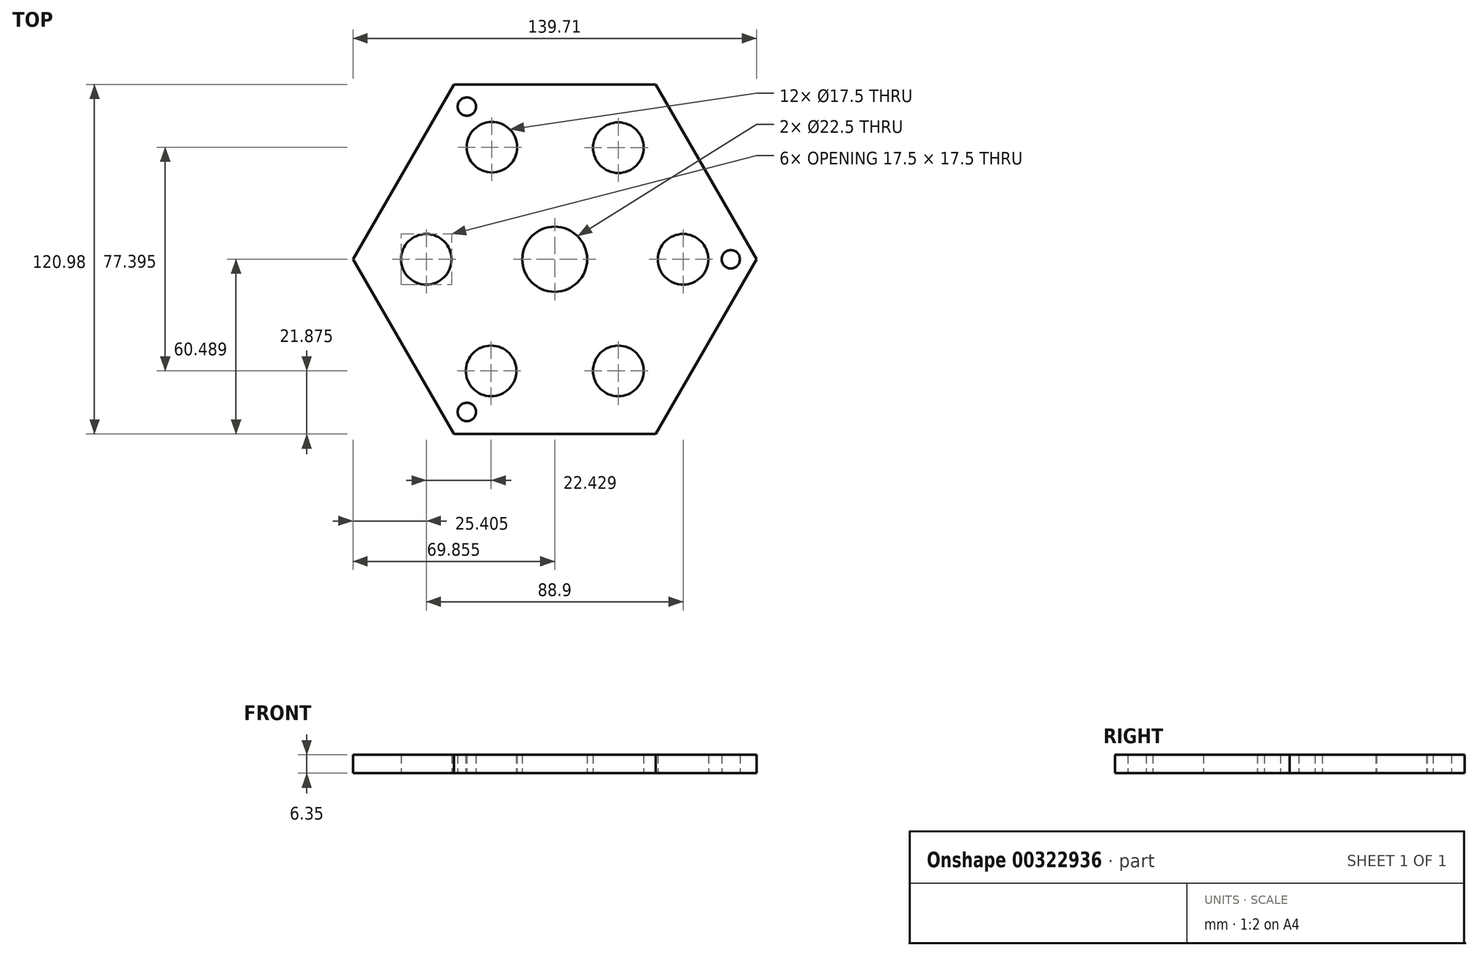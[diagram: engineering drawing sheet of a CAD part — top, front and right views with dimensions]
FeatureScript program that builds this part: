
annotation { "Feature Type Name" : "Feature", "Feature Type Description" : "" }
export const myFeature = defineFeature(function(context is Context, id is Id, definition is map)
    precondition{}
    {
        {
            var Q0;
            Q0=qCreatedBy(makeId("Top.planeOp"),FACE);
            var sketch = newSketch(context, id + "F0", { "sketchPlane" : qUnion([Q0])});
            skLineSegment(sketch, "E0.0", {"start": v(-31.75, 66) * mm, "end": v(38.1, 66) * mm});
            skLineSegment(sketch, "E0.1", {"start": v(38.1, 66) * mm, "end": v(73.02, 5.5) * mm});
            skLineSegment(sketch, "E0.2", {"start": v(73.03, 5.5) * mm, "end": v(38.1, -55) * mm});
            skLineSegment(sketch, "E0.3", {"start": v(38.1, -55) * mm, "end": v(-31.75, -55) * mm});
            skLineSegment(sketch, "E0.4", {"start": v(-31.75, -55) * mm, "end": v(-66.68, 5.5) * mm});
            skLineSegment(sketch, "E0.5", {"start": v(-66.67, 5.5) * mm, "end": v(-31.75, 66) * mm});
            skPoint(sketch, "E1", {"position": v(-41.27, 5.5) * mm});
            skPoint(sketch, "E2", {"position": v(-18.85, -33.11) * mm});
            skPoint(sketch, "E3", {"position": v(25.2, 44.11) * mm});
            skPoint(sketch, "E4", {"position": v(-18.57, 44.28) * mm});
            skPoint(sketch, "E5", {"position": v(47.62, 5.5) * mm});
            skPoint(sketch, "E6", {"position": v(25.2, -33.11) * mm});
            skPoint(sketch, "E7", {"position": v(-31.75, 66) * mm});
            skPoint(sketch, "E8", {"position": v(-27.23, 58.33) * mm});
            skPoint(sketch, "E9", {"position": v(-27.23, -47.34) * mm});
            skPoint(sketch, "E10", {"position": v(64.13, 5.5) * mm});
            skPoint(sketch, "E11", {"position": v(0, 0) * mm});
            skLineSegment(sketch, "E12", {"start": v(-18.85, -33.11) * mm, "end": v(25.2, 44.11) * mm});
            skPoint(sketch, "E13", {"position": v(3.17, 5.5) * mm});
            skSolve(sketch);
        }
        {
            var Q0;
            Q0=makeQuery(id+"F0.imprint","IMPRINT",FACE,{"disambiguationData":[TD([[makeQuery(id+"F0.imprint","IMPRINT",EDGE,{"derivedFrom":sQuery(id+"F0.wireOp",EDGE,"E0.0")}),-1.0]])]});
            extrude(context, id + "F1", {"entities" : qUnion([Q0]), "depth" : 6.35 * mm});
        }
        {
            var Q0;
            Q0=sQuery(id+"F0.wireOp",VERTEX,"E3");
            var Q1;
            Q1=sQuery(id+"F0.wireOp",VERTEX,"E5");
            var Q2;
            Q2=sQuery(id+"F0.wireOp",VERTEX,"E6");
            var Q3;
            Q3=sQuery(id+"F0.wireOp",VERTEX,"E2");
            var Q4;
            Q4=sQuery(id+"F0.wireOp",VERTEX,"E1");
            var Q5;
            Q5=sQuery(id+"F0.wireOp",VERTEX,"E4");
            var Q6;
            Q6=makeQuery(id+"F1.opExtrude","SWEPT_BODY",BODY,{"disambiguationData":[OSD([sQuery(id+"F0.wireOp",EDGE,"E0.0"),sQuery(id+"F0.wireOp",EDGE,"E0.1"),sQuery(id+"F0.wireOp",EDGE,"E0.2"),sQuery(id+"F0.wireOp",EDGE,"E0.3"),sQuery(id+"F0.wireOp",EDGE,"E0.4"),sQuery(id+"F0.wireOp",EDGE,"E0.5")])]});
            hole(context, id + "F2", {"style" : HoleStyle.SIMPLE, "endStyle" : HoleEndStyle.THROUGH, "oppositeDirection" : true, "holeDiameter" : 17.5 * mm, "tappedDepth" : 12.7 * mm, "tapClearance" : 3, "locations" : qUnion([Q0, Q1, Q2, Q3, Q4, Q5]), "scope" : qUnion([Q6])});
        }
        {
            var Q0;
            Q0=sQuery(id+"F0.wireOp",VERTEX,"E10");
            var Q1;
            Q1=sQuery(id+"F0.wireOp",VERTEX,"E9");
            var Q2;
            Q2=sQuery(id+"F0.wireOp",VERTEX,"E8");
            var Q3;
            Q3=makeQuery(id+"F1.opExtrude","SWEPT_BODY",BODY,{"disambiguationData":[OSD([sQuery(id+"F0.wireOp",EDGE,"E0.0"),sQuery(id+"F0.wireOp",EDGE,"E0.1"),sQuery(id+"F0.wireOp",EDGE,"E0.2"),sQuery(id+"F0.wireOp",EDGE,"E0.3"),sQuery(id+"F0.wireOp",EDGE,"E0.4"),sQuery(id+"F0.wireOp",EDGE,"E0.5")])]});
            hole(context, id + "F3", {"style" : HoleStyle.SIMPLE, "endStyle" : HoleEndStyle.THROUGH, "oppositeDirection" : true, "holeDiameter" : 6.35 * mm, "tappedDepth" : 12.7 * mm, "tapClearance" : 3, "locations" : qUnion([Q0, Q1, Q2]), "scope" : qUnion([Q3])});
        }
        {
            var Q0;
            Q0=sQuery(id+"F0.wireOp",VERTEX,"E13");
            var Q1;
            Q1=makeQuery(id+"F1.opExtrude","SWEPT_BODY",BODY,{"disambiguationData":[OSD([sQuery(id+"F0.wireOp",EDGE,"E0.0"),sQuery(id+"F0.wireOp",EDGE,"E0.1"),sQuery(id+"F0.wireOp",EDGE,"E0.2"),sQuery(id+"F0.wireOp",EDGE,"E0.3"),sQuery(id+"F0.wireOp",EDGE,"E0.4"),sQuery(id+"F0.wireOp",EDGE,"E0.5")])]});
            hole(context, id + "F4", {"style" : HoleStyle.SIMPLE, "endStyle" : HoleEndStyle.THROUGH, "oppositeDirection" : true, "holeDiameter" : 22.5 * mm, "tappedDepth" : 12.7 * mm, "tapClearance" : 3, "locations" : qUnion([Q0]), "scope" : qUnion([Q1])});
        }
    });
